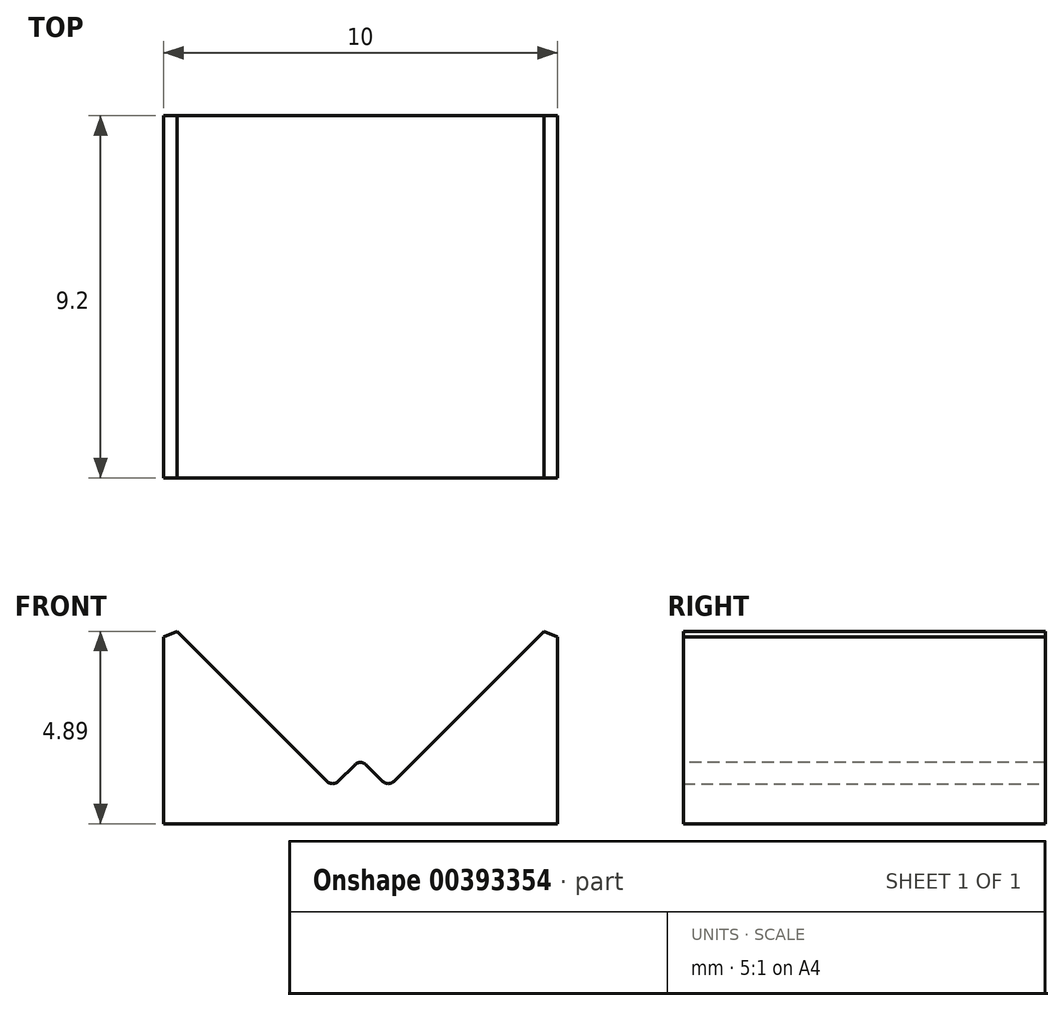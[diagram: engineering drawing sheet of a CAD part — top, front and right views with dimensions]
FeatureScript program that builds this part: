
annotation { "Feature Type Name" : "Feature", "Feature Type Description" : "" }
export const myFeature = defineFeature(function(context is Context, id is Id, definition is map)
    precondition{}
    {
        {
            var Q0;
            Q0=qCreatedBy(makeId("Front.planeOp"),FACE);
            var sketch = newSketch(context, id + "F0", { "sketchPlane" : qUnion([Q0])});
            skLineSegment(sketch, "E0.bottom", {"start": v(0, 0) * mm, "end": v(10, 0) * mm});
            skLineSegment(sketch, "E0.left", {"start": v(0, 0) * mm, "end": v(0, 5.25) * mm});
            skLineSegment(sketch, "E0.right", {"start": v(10, 0) * mm, "end": v(10, 5.25) * mm});
            skPoint(sketch, "E1.endSnap0", {"position": v(5, 5.25) * mm});
            skCircle(sketch, "E2", {"center": v(5, 7.3) * mm, "radius": 4 * mm});
            skLineSegment(sketch, "E3", {"start": v(7.83, 4.47) * mm, "end": v(4.3, 0.94) * mm});
            skLineSegment(sketch, "E4", {"start": v(2.17, 4.47) * mm, "end": v(5.7, 0.94) * mm});
            skLineSegment(sketch, "E5", {"start": v(2.17, 4.47) * mm, "end": v(1.4, 5.25) * mm});
            skLineSegment(sketch, "E6", {"start": v(7.83, 4.47) * mm, "end": v(8.6, 5.25) * mm});
            skPoint(sketch, "E1.start.orphan", {"position": v(5, 0) * mm});
            skPoint(sketch, "E7.start.orphan", {"position": v(4.3, 2.35) * mm});
            skPoint(sketch, "E8.end.orphan", {"position": v(5.7, 2.35) * mm});
            skLineSegment(sketch, "E9.0", {"start": v(10, 5.23) * mm, "end": v(5.7, 0.94) * mm});
            skLineSegment(sketch, "E10.0", {"start": v(0, 5.23) * mm, "end": v(4.3, 0.94) * mm});
            skLineSegment(sketch, "E11", {"start": v(8.6, 5.25) * mm, "end": v(9.31, 4.54) * mm});
            skLineSegment(sketch, "E12", {"start": v(1.4, 5.25) * mm, "end": v(0.69, 4.54) * mm});
            skSolve(sketch);
        }
        {
            var Q0;
            {var subQ1=sQuery(id+"F0.wireOp",EDGE,"E0.bottom");Q0=makeQuery(id+"F0.imprint","IMPRINT",FACE,{"disambiguationData":[TD([[makeQuery(id+"F0.imprint","IMPRINT",EDGE,{"derivedFrom":subQ1}),1.0]])]});}
            extrude(context, id + "F1", {"entities" : qUnion([Q0]), "endBound" : BoundingType.SYMMETRIC, "depth" : 9.2 * mm});
        }
        {
            var Q0;
            Q0=makeQuery(id+"F1.opExtrude","SWEPT_EDGE",EDGE,{"disambiguationData":[OSD([sQuery(id+"F0.wireOp",EDGE,"E0.left"),sQuery(id+"F0.wireOp",EDGE,"E10.0")])]});
            chamfer(context, id + "F2", {"entities" : qUnion([Q0]), "width" : 0.2 * mm, "tangentPropagation" : true});
        }
        {
            var Q0;
            Q0=makeQuery(id+"F1.opExtrude","SWEPT_EDGE",EDGE,{"disambiguationData":[OSD([sQuery(id+"F0.wireOp",EDGE,"E0.right"),sQuery(id+"F0.wireOp",EDGE,"E9.0")])]});
            chamfer(context, id + "F3", {"entities" : qUnion([Q0]), "width" : 0.2 * mm, "tangentPropagation" : true});
        }
        {
            var Q0;
            Q0=makeQuery(id+"F1.opExtrude","SWEPT_EDGE",EDGE,{"disambiguationData":[OSD([sQuery(id+"F0.wireOp",EDGE,"E3"),sQuery(id+"F0.wireOp",EDGE,"E10.0")])]});
            var Q1;
            Q1=makeQuery(id+"F1.opExtrude","SWEPT_EDGE",EDGE,{"disambiguationData":[OSD([sQuery(id+"F0.wireOp",EDGE,"E3"),sQuery(id+"F0.wireOp",EDGE,"E4")])]});
            var Q2;
            Q2=makeQuery(id+"F1.opExtrude","SWEPT_EDGE",EDGE,{"disambiguationData":[OSD([sQuery(id+"F0.wireOp",EDGE,"E4"),sQuery(id+"F0.wireOp",EDGE,"E9.0")])]});
            fillet(context, id + "F4", {"entities" : qUnion([Q0, Q1, Q2]), "radius" : 0.2 * mm, "tangentPropagation" : true, "allowEdgeOverflow" : false});
        }
    });
